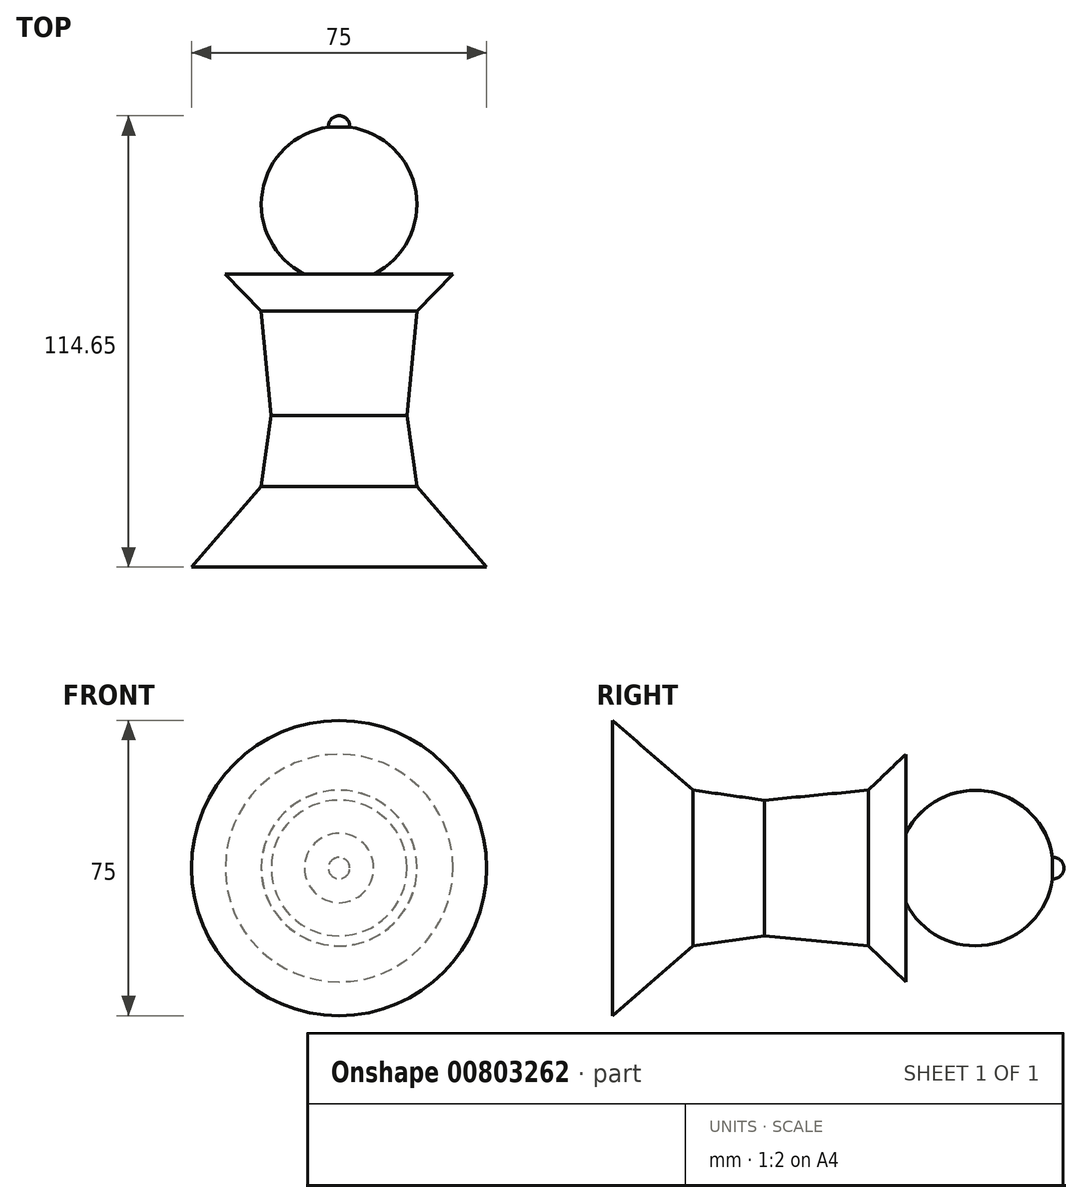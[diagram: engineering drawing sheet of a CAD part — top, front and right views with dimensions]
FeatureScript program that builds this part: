
annotation { "Feature Type Name" : "Feature", "Feature Type Description" : "" }
export const myFeature = defineFeature(function(context is Context, id is Id, definition is map)
    precondition{}
    {
        {
            var Q0;
            Q0=qCreatedBy(makeId("Top.planeOp"),FACE);
            var sketch = newSketch(context, id + "F0", { "sketchPlane" : qUnion([Q0])});
            skLineSegment(sketch, "E0", {"start": v(0, 74.83) * mm, "end": v(0, -74.28) * mm, "construction": true});
            skArc(sketch, "E1", {"start": v(8.8, 19.71) * mm, "mid": v(19.5, 40.6) * mm, "end": v(2.71, 57) * mm});
            skLineSegment(sketch, "E2.bottom", {"start": v(8.8, 19.71) * mm, "end": v(19.8, 19.71) * mm});
            skLineSegment(sketch, "E2.left", {"start": v(0, 19.71) * mm, "end": v(0, -34.31) * mm});
            skLineSegment(sketch, "E3", {"start": v(19.8, -34.31) * mm, "end": v(37.5, -54.75) * mm});
            skLineSegment(sketch, "E4", {"start": v(37.5, -54.75) * mm, "end": v(0, -54.75) * mm});
            skLineSegment(sketch, "E5", {"start": v(0, 74.83) * mm, "end": v(0, -74.28) * mm});
            skArc(sketch, "E6", {"start": v(2.71, 57) * mm, "mid": v(1.99, 59.04) * mm, "end": v(0, 59.9) * mm});
            skLineSegment(sketch, "E7", {"start": v(8.8, 19.71) * mm, "end": v(28.93, 19.71) * mm});
            skLineSegment(sketch, "E8", {"start": v(28.93, 19.71) * mm, "end": v(19.8, 10.22) * mm});
            skLineSegment(sketch, "E9", {"start": v(19.8, 10.22) * mm, "end": v(17.25, -16.24) * mm});
            skLineSegment(sketch, "E10", {"start": v(17.25, -16.24) * mm, "end": v(19.8, -34.31) * mm});
            skSolve(sketch);
        }
        {
            var Q0;
            {var subQ1=sQuery(id+"F0.wireOp",EDGE,"E1");Q0=makeQuery(id+"F0.imprint","IMPRINT",FACE,{"disambiguationData":[TD([[makeQuery(id+"F0.imprint","IMPRINT",EDGE,{"derivedFrom":subQ1}),1.0]])]});}
            var Q1;
            Q1=sQuery(id+"F0.wireOp",EDGE,"E5");
            revolve(context, id + "F1", {"surfaceOperationType" : NewSurfaceOperationType.NEW, "entities" : qUnion([Q0]), "axis" : qUnion([Q1]), "revolveType" : RevolveType.FULL});
        }
    });
